# Revit family: Haworth_Massimosistema_ChaiseLounge
name_source: partatom
category: Furniture
revit_build: Autodesk Revit 2018 (Build: 20170223_1515(x64)
units: mm (PartAtom-declared; Revit-internal decimal feet)

## family parameters
Always vertical = Yes
Cut with Voids When Loaded = No
OmniClass Number = 23.40.20.00
OmniClass Title = General Furniture and Specialties
Room Calculation Point = No
Shared = No
Work Plane-Based = No

## types (2) — shared parameters
Actual Depth = 71 3/4"
Actual Height = 33 3/4"
Arm Height = 22 3/4"
Arm Width = 8 3/4"
Assembly Code = E2020200
Frame Finish = Haworth _ Paint _ Metallic Gunmetal
Manufacturer = Haworth
Model = HCPF-MSHX
Seat Depth = 55"
Seat Height = 16 1/2"
Size = Verify Final Dim. w/ Haworth
URL = http://www.haworth.com
URL - Product = http://www.haworth.com
Version = 1
Warranty = https://www.haworth.com

## per-type parameters (varying)
| type | Actual Width | Back Arm Width | Bottom Cushion | Cushion Width | Description | Two Seat Control | With Arms | Without Arms |
| HCPF-MSHX-00 | 33 1/2" | 33 1/2" | 33 1/2" | 33 1/2" | Haworth Massimosistema Sofa - Chaise Lounge - Armless | No | No | Yes |
| HCPF-MSHX-0L | 41" | 41" | 32 1/4" | 32 1/4" | Haworth Massimosistema Sofa - Chaise Lounge - Low One Arm | Yes | Yes | No |

## geometry (parser evidence)
native form markers: Sweep x10
no freeform markers — native parametric forms only
